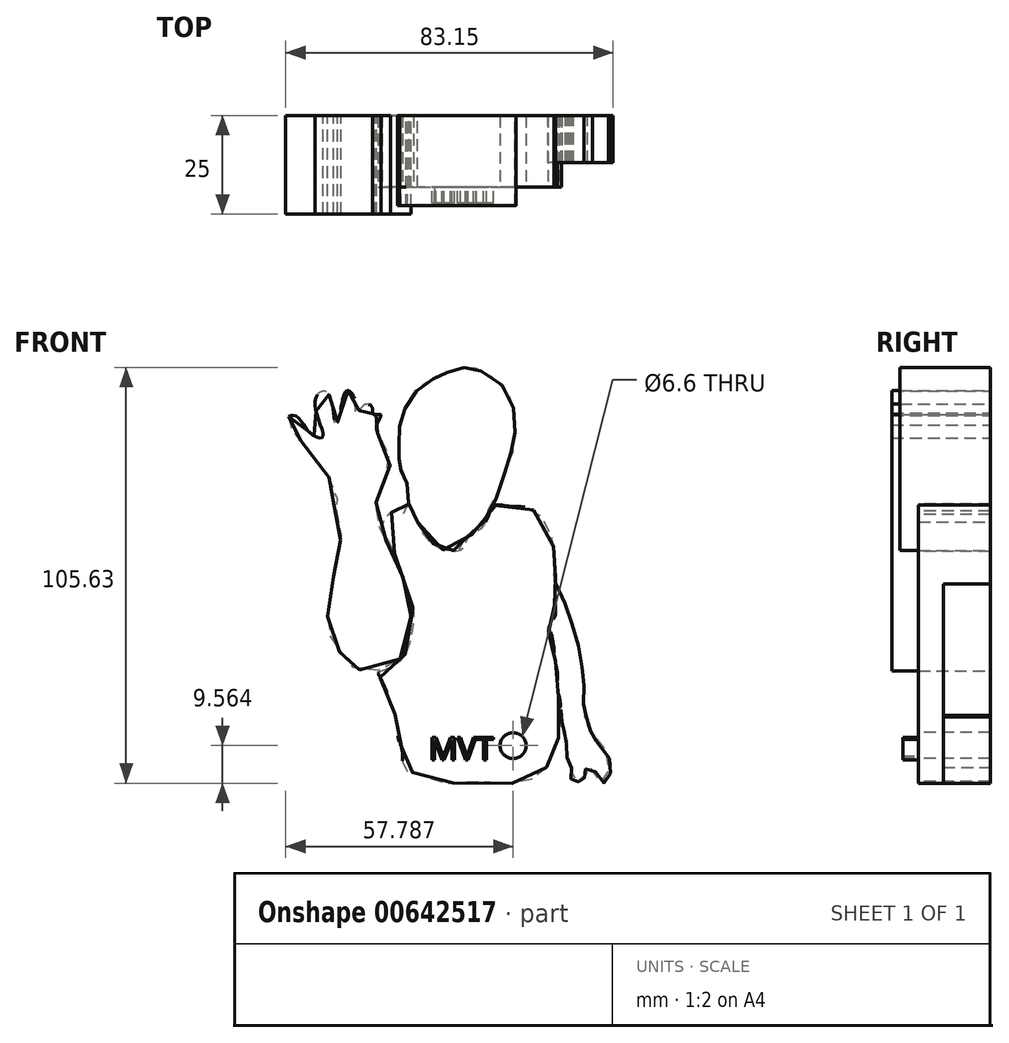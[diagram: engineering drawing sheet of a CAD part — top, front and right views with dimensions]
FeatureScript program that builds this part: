
annotation { "Feature Type Name" : "Feature", "Feature Type Description" : "" }
export const myFeature = defineFeature(function(context is Context, id is Id, definition is map)
    precondition{}
    {
        {
            var Q0;
            Q0=qCreatedBy(makeId("Front.planeOp"),FACE);
            var sketch = newSketch(context, id + "F0", { "sketchPlane" : qUnion([Q0])});
            skFitSpline(sketch, "E0", {"points": [v(-38.61, 40.45) * mm, v(-39.36, 39.39) * mm, v(-37.12, 36.4) * mm, v(-33.38, 31.39) * mm, v(-28.37, 24.98) * mm, v(-26.24, 19.86) * mm, v(-27.1, 18.8) * mm, v(-26.56, 16.34) * mm, v(-25.28, 12.07) * mm, v(-26.02, 6) * mm, v(-26.77, 1.3) * mm, v(-27.84, -2.86) * mm, v(-28.7, -9.48) * mm, v(-27.97, -15.46) * mm, v(-25.6, -19.38) * mm, v(-23.84, -20.99) * mm, v(-22.53, -23.03) * mm, v(-17.01, -24.13) * mm, v(-10.8, -21.67) * mm, v(-8.18, -16.27) * mm, v(-7.52, -8.1) * mm, v(-8.67, -2.86) * mm, v(-10.8, 2.54) * mm, v(-13.41, 8.1) * mm, v(-15.87, 13.34) * mm, v(-16.36, 18.9) * mm, v(-14.23, 24.3) * mm, v(-12.76, 29.37) * mm, v(-14.72, 33.95) * mm, v(-16.2, 37.06) * mm, v(-15.87, 39.18) * mm, v(-15.21, 40.98) * mm, v(-17.01, 40.98) * mm, v(-17.34, 42.78) * mm, v(-19.3, 43.44) * mm, v(-21.43, 41.31) * mm, v(-21.92, 45.07) * mm, v(-23.72, 47.04) * mm, v(-25.03, 43.93) * mm, v(-26.17, 39.02) * mm, v(-26.66, 38.37) * mm, v(-27.64, 44.25) * mm, v(-29.44, 46.87) * mm, v(-31.4, 45.9) * mm, v(-31.24, 40.33) * mm, v(-29.93, 35.26) * mm, v(-33.04, 36.24) * mm, v(-36.64, 40.5) * mm, v(-38.61, 40.45) * mm]});
            skSolve(sketch);
        }
        {
            var Q0;
            Q0=qCreatedBy(makeId("Front.planeOp"),FACE);
            var sketch = newSketch(context, id + "F1", { "sketchPlane" : qUnion([Q0])});
            skFitSpline(sketch, "E1", {"points": [v(6.41, 9.57) * mm, v(9.3, 12) * mm, v(10.97, 13.82) * mm, v(12.79, 17.92) * mm, v(14.46, 20.2) * mm, v(15.67, 24.3) * mm, v(16.73, 27.94) * mm, v(17.19, 30.97) * mm, v(18.55, 31.58) * mm, v(18.86, 34.16) * mm, v(19, 37.53) * mm, v(19, 40.87) * mm, v(17.97, 44.32) * mm, v(16.48, 47.54) * mm, v(13.26, 50.41) * mm, v(10.5, 51.9) * mm, v(8.79, 52.67) * mm, v(7.41, 52.83) * mm, v(5.73, 52.9) * mm, v(3.75, 52.67) * mm, v(2.22, 51.83) * mm, v(0.93, 51.45) * mm, v(0, 51.07) * mm, v(-1.29, 50.38) * mm, v(-2.81, 49.4) * mm, v(-5.03, 48.1) * mm, v(-6.78, 46.11) * mm, v(-8.39, 43.97) * mm, v(-9.07, 42.3) * mm, v(-9.68, 40.16) * mm, v(-10.3, 38.48) * mm, v(-10.45, 36.57) * mm, v(-10.45, 34.2) * mm, v(-10.52, 33.37) * mm, v(-10.9, 32.45) * mm, v(-10.67, 30.92) * mm, v(-10.52, 30) * mm, v(-10.45, 28.79) * mm, v(-10.3, 28.25) * mm, v(-10.3, 27.87) * mm, v(-10.06, 27.18) * mm, v(-10.06, 26.11) * mm, v(-8.61, 25.58) * mm, v(-8.54, 23.56) * mm, v(-8.75, 21.43) * mm, v(-8.54, 19.4) * mm, v(-7.26, 16.84) * mm, v(-6.08, 14.17) * mm, v(-4.59, 11.61) * mm, v(-2.67, 8.95) * mm, v(0, 6.92) * mm, v(2.35, 6.5) * mm, v(4.48, 6.6) * mm, v(5.01, 7.24) * mm, v(6.41, 9.57) * mm]});
            skSolve(sketch);
        }
        {
            var Q0;
            Q0=qCreatedBy(makeId("Front.planeOp"),FACE);
            var sketch = newSketch(context, id + "F2", { "sketchPlane" : qUnion([Q0])});
            skFitSpline(sketch, "E2", {"points": [v(-8.01, 18.3) * mm, v(-8.96, 16.96) * mm, v(-9.72, 15.63) * mm, v(-11.05, 16.4) * mm, v(-12.38, 16.2) * mm, v(-14.86, 13.54) * mm, v(-12.38, 7.08) * mm, v(-9.15, -1.48) * mm, v(-6.87, -9.08) * mm, v(-7.44, -14.97) * mm, v(-9.34, -20.49) * mm, v(-14.1, -23.9) * mm, v(-15.8, -24.48) * mm, v(-14.27, -28) * mm, v(-12.88, -32.5) * mm, v(-11.67, -35.1) * mm, v(-10.65, -39.15) * mm, v(-10.82, -41) * mm, v(-9.98, -43.34) * mm, v(-9.81, -47.36) * mm, v(-10.15, -48.7) * mm, v(-7.45, -49.9) * mm, v(-3.55, -51.12) * mm, v(0, -52.59) * mm, v(10.34, -52.22) * mm, v(17.9, -52.7) * mm, v(23.14, -51.61) * mm, v(25.33, -49.3) * mm, v(27.65, -48.2) * mm, v(28.38, -45.64) * mm, v(29.96, -42.96) * mm, v(29.84, -38.94) * mm, v(30.7, -35.04) * mm, v(29.84, -30.29) * mm, v(29.72, -27.12) * mm, v(29.35, -23.95) * mm, v(28.99, -20.17) * mm, v(28.5, -17.5) * mm, v(28.13, -15.06) * mm, v(27.4, -14.33) * mm, v(27.65, -12.62) * mm, v(28.86, -10.55) * mm, v(28.99, -8.48) * mm, v(29.1, -5.43) * mm, v(29.1, -3.24) * mm, v(29.1, -1.9) * mm, v(29.1, 0) * mm, v(28.62, 1.4) * mm, v(28.74, 2.73) * mm, v(28.8, 6.56) * mm, v(27.7, 11.9) * mm, v(24.87, 15.83) * mm, v(21.73, 17.4) * mm, v(17.02, 17.71) * mm, v(13.88, 17.87) * mm, v(12, 14.88) * mm, v(9.8, 11.58) * mm, v(6.8, 9.54) * mm, v(5.7, 6.87) * mm, v(1.3, 6.4) * mm, v(-2.46, 8.6) * mm, v(-4.98, 11.74) * mm, v(-6.23, 14.88) * mm, v(-8.01, 18.3) * mm]});
            skSolve(sketch);
        }
        {
            var Q0;
            Q0=qCreatedBy(makeId("Front.planeOp"),FACE);
            var sketch = newSketch(context, id + "F3", { "sketchPlane" : qUnion([Q0])});
            skFitSpline(sketch, "E3", {"points": [v(29.35, -2.03) * mm, v(31.07, -5.73) * mm, v(32.79, -10.36) * mm, v(34.24, -14.98) * mm, v(35.43, -19.6) * mm, v(35.96, -23.7) * mm, v(36.35, -27) * mm, v(36.35, -30.04) * mm, v(36.35, -33.87) * mm, v(36.62, -35.85) * mm, v(37.15, -35.46) * mm, v(38.47, -39.16) * mm, v(37.4, -39.55) * mm, v(39.4, -41.93) * mm, v(42.83, -45.76) * mm, v(42.7, -48) * mm, v(43.09, -49.99) * mm, v(43.62, -52.37) * mm, v(40.18, -52.1) * mm, v(39.66, -50.52) * mm, v(38.6, -49.06) * mm, v(37.28, -48.67) * mm, v(36.75, -49.33) * mm, v(36.48, -49.99) * mm, v(36.48, -50.91) * mm, v(36.62, -51.57) * mm, v(36.62, -52.23) * mm, v(35.43, -52.37) * mm, v(34.37, -52.37) * mm, v(32.79, -52.37) * mm, v(33.71, -50.78) * mm, v(33.31, -49.72) * mm, v(33.31, -48.54) * mm, v(33.18, -47.48) * mm, v(32.26, -46.29) * mm, v(31.73, -44.44) * mm, v(32, -42.85) * mm, v(32.26, -41.27) * mm, v(31.6, -39.95) * mm, v(30.8, -39.42) * mm, v(30.67, -37.83) * mm, v(30.94, -36.9) * mm, v(30.94, -35.85) * mm, v(30.54, -33.34) * mm, v(30.28, -31.23) * mm, v(29.61, -28.32) * mm, v(29.75, -25.28) * mm, v(29.09, -21.58) * mm, v(28.82, -18.68) * mm, v(28.43, -16.04) * mm, v(27.9, -14.32) * mm, v(27.24, -13.53) * mm, v(28.43, -11.28) * mm, v(29.22, -9.83) * mm, v(29.09, -6.52) * mm, v(29.09, -4.8) * mm, v(29.35, -2.03) * mm]});
            skSolve(sketch);
        }
        {
            var Q0;
            Q0=makeQuery(id+"F0.imprint","IMPRINT",FACE,{"disambiguationData":[TD([[makeQuery(id+"F0.imprint","IMPRINT",EDGE,{"derivedFrom":sQuery(id+"F0.wireOp",EDGE,"E0")}),1.0]])]});
            extrude(context, id + "F4", {"entities" : qUnion([Q0]), "depth" : 25 * mm, "offsetDistance" : 25 * mm});
        }
        {
            var Q0;
            Q0=makeQuery(id+"F1.imprint","IMPRINT",FACE,{"disambiguationData":[TD([[makeQuery(id+"F1.imprint","IMPRINT",EDGE,{"derivedFrom":sQuery(id+"F1.wireOp",EDGE,"E1")}),1.0]])]});
            extrude(context, id + "F5", {"entities" : qUnion([Q0]), "depth" : 22.9 * mm, "offsetDistance" : 25 * mm});
        }
        {
            var Q0;
            Q0=makeQuery(id+"F2.imprint","IMPRINT",FACE,{"disambiguationData":[TD([[makeQuery(id+"F2.imprint","IMPRINT",EDGE,{"derivedFrom":sQuery(id+"F2.wireOp",EDGE,"E2")}),1.0]])]});
            extrude(context, id + "F6", {"entities" : qUnion([Q0]), "operationType" : NewBodyOperationType.ADD, "depth" : 18.2 * mm, "offsetDistance" : 25 * mm});
        }
        {
            var Q0;
            Q0 = qSketchRegion(id + "F3", true);
            extrude(context, id + "F7", {"entities" : qUnion([Q0]), "depth" : 11.9 * mm, "offsetDistance" : 25 * mm});
        }
        {
            var Q0;
            Q0=makeQuery(id+"F6.opExtrude","CAP_FACE",FACE,{"disambiguationData":[OSD([sQuery(id+"F2.wireOp",EDGE,"E2")])],"isStart":false});
            var sketch = newSketch(context, id + "F8", { "sketchPlane" : qUnion([Q0])});
            skText(sketch, "E4", { "text": "MVT", "fontName": "OpenSans-Regular.ttf"});
            const initialGuessF8  = {"E4": [-0.00293, -0.04675, 1, 0, 0.00577]};
            skSetInitialGuess(sketch, initialGuessF8);
            skSolve(sketch);
        }
        {
            var Q0;
            Q0 = qSketchRegion(id + "F8", true);
            extrude(context, id + "F9", {"entities" : qUnion([Q0]), "operationType" : NewBodyOperationType.ADD, "depth" : 4 * mm, "offsetDistance" : 25 * mm});
        }
        {
            var Q0;
            Q0=makeQuery(id+"F6.opExtrude","CAP_FACE",FACE,{"disambiguationData":[OSD([sQuery(id+"F2.wireOp",EDGE,"E2")])],"isStart":false});
            var sketch = newSketch(context, id + "F10", { "sketchPlane" : qUnion([Q0])});
            skCircle(sketch, "E5", {"center": v(18.43, -43.16) * mm, "radius": 3.3 * mm});
            skSolve(sketch);
        }
        {
            var Q0;
            Q0=makeQuery(id+"F10.imprint","IMPRINT",FACE,{"disambiguationData":[TD([[makeQuery(id+"F10.imprint","IMPRINT",EDGE,{"derivedFrom":sQuery(id+"F10.wireOp",EDGE,"E5")}),1.0]])]});
            extrude(context, id + "F11", {"entities" : qUnion([Q0]), "operationType" : NewBodyOperationType.REMOVE, "endBound" : BoundingType.UP_TO_NEXT, "oppositeDirection" : true, "depth" : 25 * mm, "offsetDistance" : 25 * mm});
        }
    });
